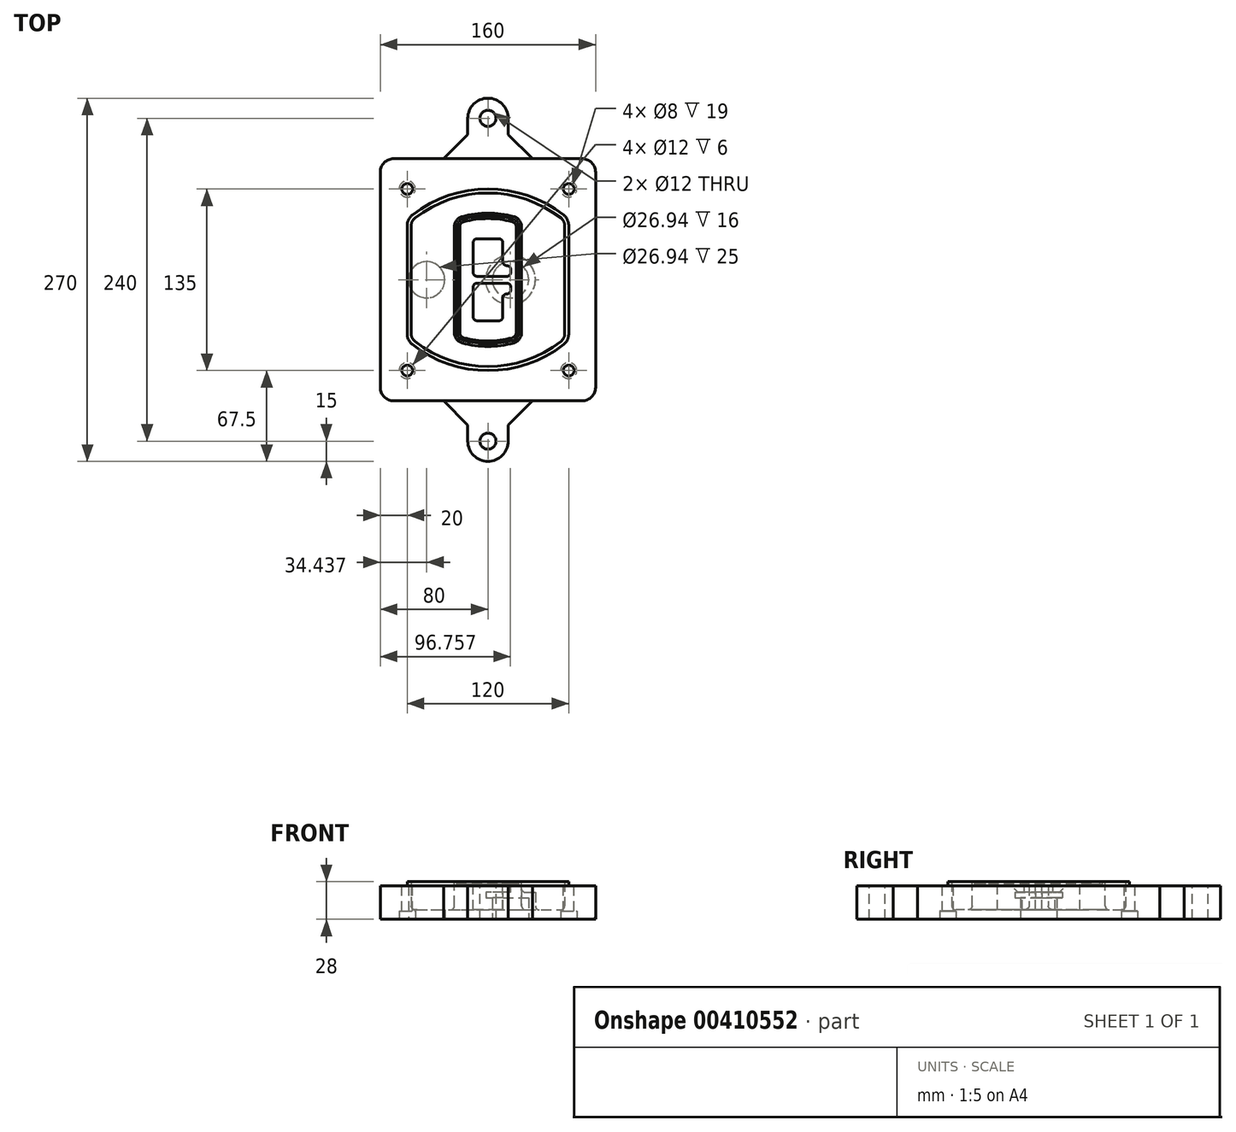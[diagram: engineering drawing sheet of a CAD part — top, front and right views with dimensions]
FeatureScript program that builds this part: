
annotation { "Feature Type Name" : "Feature", "Feature Type Description" : "" }
export const myFeature = defineFeature(function(context is Context, id is Id, definition is map)
    precondition{}
    {
        {
            var Q0;
            Q0=qCreatedBy(makeId("Top.planeOp"),FACE);
            var sketch = newSketch(context, id + "F0", { "sketchPlane" : qUnion([Q0])});
            skPoint(sketch, "E0.rect.middle", {"position": v(0, 0) * mm});
            skLineSegment(sketch, "E1.bottom", {"start": v(-70, -90) * mm, "end": v(70, -90) * mm});
            skLineSegment(sketch, "E1.top", {"start": v(-70, 90) * mm, "end": v(70, 90) * mm});
            skLineSegment(sketch, "E1.left", {"start": v(-80, -80) * mm, "end": v(-80, 80) * mm});
            skLineSegment(sketch, "E1.right", {"start": v(80, -80) * mm, "end": v(80, 80) * mm});
            skLineSegment(sketch, "E2", {"start": v(-80, 90) * mm, "end": v(80, -90) * mm, "construction": true});
            skLineSegment(sketch, "E3", {"start": v(80, 90) * mm, "end": v(-80, -90) * mm, "construction": true});
            skCircle(sketch, "E4", {"center": v(-60, 67.5) * mm, "radius": 4 * mm});
            skCircle(sketch, "E5", {"center": v(60, 67.5) * mm, "radius": 4 * mm});
            skCircle(sketch, "E6", {"center": v(60, -67.5) * mm, "radius": 4 * mm});
            skCircle(sketch, "E7", {"center": v(-60, -67.5) * mm, "radius": 4 * mm});
            skLineSegment(sketch, "E8", {"start": v(-60, 67.5) * mm, "end": v(60, 67.5) * mm, "construction": true});
            skLineSegment(sketch, "E9", {"start": v(60, 67.5) * mm, "end": v(60, -67.5) * mm, "construction": true});
            skLineSegment(sketch, "E10", {"start": v(60, -67.5) * mm, "end": v(-60, -67.5) * mm, "construction": true});
            skLineSegment(sketch, "E11", {"start": v(-60, -67.5) * mm, "end": v(-60, 67.5) * mm, "construction": true});
            skLineSegment(sketch, "E12", {"start": v(-60, 40.3) * mm, "end": v(-60, -40.3) * mm});
            skLineSegment(sketch, "E13", {"start": v(60, 40.3) * mm, "end": v(60, -40.3) * mm});
            skArc(sketch, "E14", {"start": v(56.15, 48.18) * mm, "mid": v(0, 67.5) * mm, "end": v(-56.15, 48.18) * mm});
            skArc(sketch, "E15", {"start": v(-56.15, -48.18) * mm, "mid": v(0, -67.5) * mm, "end": v(56.15, -48.18) * mm});
            skLineSegment(sketch, "E16", {"start": v(-60, 0) * mm, "end": v(60, 0) * mm, "construction": true});
            skPoint(sketch, "E17.visualSharp", {"position": v(-60, -45) * mm});
            skArc(sketch, "E17.filletArc", {"start": v(-60, -40.3) * mm, "mid": v(-58.99, -44.68) * mm, "end": v(-56.15, -48.18) * mm});
            skPoint(sketch, "E18.visualSharp", {"position": v(-60, 45) * mm});
            skArc(sketch, "E18.filletArc", {"start": v(-56.15, 48.18) * mm, "mid": v(-58.99, 44.68) * mm, "end": v(-60, 40.3) * mm});
            skPoint(sketch, "E19.visualSharp", {"position": v(60, 45) * mm});
            skArc(sketch, "E19.filletArc", {"start": v(60, 40.3) * mm, "mid": v(58.99, 44.68) * mm, "end": v(56.15, 48.18) * mm});
            skPoint(sketch, "E20.visualSharp", {"position": v(60, -45) * mm});
            skArc(sketch, "E20.filletArc", {"start": v(56.15, -48.18) * mm, "mid": v(58.99, -44.68) * mm, "end": v(60, -40.3) * mm});
            skPoint(sketch, "E21.visualSharp", {"position": v(-80, 90) * mm});
            skArc(sketch, "E21.filletArc", {"start": v(-70, 90) * mm, "mid": v(-77.07, 87.07) * mm, "end": v(-80, 80) * mm});
            skPoint(sketch, "E22.visualSharp", {"position": v(80, 90) * mm});
            skArc(sketch, "E22.filletArc", {"start": v(80, 80) * mm, "mid": v(77.07, 87.07) * mm, "end": v(70, 90) * mm});
            skPoint(sketch, "E23.visualSharp", {"position": v(80, -90) * mm});
            skArc(sketch, "E23.filletArc", {"start": v(70, -90) * mm, "mid": v(77.07, -87.07) * mm, "end": v(80, -80) * mm});
            skPoint(sketch, "E24.visualSharp", {"position": v(-80, -90) * mm});
            skArc(sketch, "E24.filletArc", {"start": v(-80, -80) * mm, "mid": v(-77.07, -87.07) * mm, "end": v(-70, -90) * mm});
            skArc(sketch, "E25.0", {"start": v(57, 40.3) * mm, "mid": v(56.3, 43.36) * mm, "end": v(54.3, 45.81) * mm});
            skLineSegment(sketch, "E25.1", {"start": v(57, 40.3) * mm, "end": v(57, -40.3) * mm});
            skArc(sketch, "E25.2", {"start": v(54.3, -45.81) * mm, "mid": v(56.3, -43.36) * mm, "end": v(57, -40.3) * mm});
            skArc(sketch, "E25.3", {"start": v(-54.3, -45.81) * mm, "mid": v(0, -64.5) * mm, "end": v(54.3, -45.81) * mm});
            skArc(sketch, "E25.4", {"start": v(-57, -40.3) * mm, "mid": v(-56.3, -43.36) * mm, "end": v(-54.3, -45.81) * mm});
            skArc(sketch, "E25.5", {"start": v(54.3, 45.81) * mm, "mid": v(0, 64.5) * mm, "end": v(-54.3, 45.81) * mm});
            skLineSegment(sketch, "E25.6", {"start": v(-57, 40.3) * mm, "end": v(-57, -40.3) * mm});
            skArc(sketch, "E25.7", {"start": v(-54.3, 45.81) * mm, "mid": v(-56.3, 43.36) * mm, "end": v(-57, 40.3) * mm});
            skArc(sketch, "E26.0", {"start": v(-58.62, 51.33) * mm, "mid": v(-62.58, 46.43) * mm, "end": v(-64, 40.3) * mm});
            skArc(sketch, "E26.1", {"start": v(58.62, 51.33) * mm, "mid": v(0, 71.5) * mm, "end": v(-58.62, 51.33) * mm});
            skArc(sketch, "E26.2", {"start": v(64, 40.3) * mm, "mid": v(62.58, 46.43) * mm, "end": v(58.62, 51.33) * mm});
            skLineSegment(sketch, "E26.3", {"start": v(64, 40.3) * mm, "end": v(64, -40.3) * mm});
            skArc(sketch, "E26.4", {"start": v(58.62, -51.33) * mm, "mid": v(62.58, -46.43) * mm, "end": v(64, -40.3) * mm});
            skLineSegment(sketch, "E26.5", {"start": v(-64, 40.3) * mm, "end": v(-64, -40.3) * mm});
            skArc(sketch, "E26.6", {"start": v(-58.62, -51.33) * mm, "mid": v(0, -71.5) * mm, "end": v(58.62, -51.33) * mm});
            skArc(sketch, "E26.7", {"start": v(-64, -40.3) * mm, "mid": v(-62.58, -46.43) * mm, "end": v(-58.62, -51.33) * mm});
            skSolve(sketch);
        }
        {
            var Q0;
            Q0=makeQuery(id+"F0.imprint","IMPRINT",FACE,{"disambiguationData":[TD([[makeQuery(id+"F0.imprint","IMPRINT",EDGE,{"derivedFrom":sQuery(id+"F0.wireOp",EDGE,"E1.bottom")}),1.0]])]});
            var Q1;
            Q1=makeQuery(id+"F0.imprint","IMPRINT",FACE,{"disambiguationData":[TD([[makeQuery(id+"F0.imprint","IMPRINT",EDGE,{"derivedFrom":sQuery(id+"F0.wireOp",EDGE,"E12")}),1.0]])]});
            var Q2;
            Q2=makeQuery(id+"F0.imprint","IMPRINT",FACE,{"disambiguationData":[TD([[makeQuery(id+"F0.imprint","IMPRINT",EDGE,{"derivedFrom":sQuery(id+"F0.wireOp",EDGE,"E25.0")}),1.0]])]});
            var Q3;
            Q3=makeQuery(id+"F0.imprint","IMPRINT",FACE,{"disambiguationData":[TD([[makeQuery(id+"F0.imprint","IMPRINT",EDGE,{"derivedFrom":sQuery(id+"F0.wireOp",EDGE,"E12")}),-1.0]])]});
            extrude(context, id + "F1", {"entities" : qUnion([Q0, Q1, Q2, Q3]), "oppositeDirection" : true, "depth" : 25 * mm});
        }
        {
            var Q0;
            Q0=makeQuery(id+"F0.imprint","IMPRINT",FACE,{"disambiguationData":[TD([[makeQuery(id+"F0.imprint","IMPRINT",EDGE,{"derivedFrom":sQuery(id+"F0.wireOp",EDGE,"E12")}),1.0]])]});
            extrude(context, id + "F2", {"entities" : qUnion([Q0]), "operationType" : NewBodyOperationType.ADD, "depth" : 3 * mm});
        }
        {
            var Q0;
            Q0=makeQuery(id+"F0.imprint","IMPRINT",FACE,{"disambiguationData":[TD([[makeQuery(id+"F0.imprint","IMPRINT",EDGE,{"derivedFrom":sQuery(id+"F0.wireOp",EDGE,"E25.0")}),1.0]])]});
            extrude(context, id + "F3", {"entities" : qUnion([Q0]), "operationType" : NewBodyOperationType.REMOVE, "oppositeDirection" : true, "depth" : 18 * mm});
        }
        {
            var Q0;
            Q0=makeQuery(id+"F2.opExtrude","CAP_FACE",FACE,{"disambiguationData":[OSD([sQuery(id+"F0.wireOp",EDGE,"E12"),sQuery(id+"F0.wireOp",EDGE,"E13"),sQuery(id+"F0.wireOp",EDGE,"E14"),sQuery(id+"F0.wireOp",EDGE,"E15"),sQuery(id+"F0.wireOp",EDGE,"E17.filletArc"),sQuery(id+"F0.wireOp",EDGE,"E18.filletArc"),sQuery(id+"F0.wireOp",EDGE,"E19.filletArc"),sQuery(id+"F0.wireOp",EDGE,"E20.filletArc"),sQuery(id+"F0.wireOp",EDGE,"E25.0"),sQuery(id+"F0.wireOp",EDGE,"E25.1"),sQuery(id+"F0.wireOp",EDGE,"E25.2"),sQuery(id+"F0.wireOp",EDGE,"E25.3"),sQuery(id+"F0.wireOp",EDGE,"E25.4"),sQuery(id+"F0.wireOp",EDGE,"E25.5"),sQuery(id+"F0.wireOp",EDGE,"E25.6"),sQuery(id+"F0.wireOp",EDGE,"E25.7")])],"isStart":false});
            var sketch = newSketch(context, id + "F4", { "sketchPlane" : qUnion([Q0])});
            skArc(sketch, "E27.0", {"start": v(-19.08, -46.97) * mm, "mid": v(0, -49.5) * mm, "end": v(19.08, -46.97) * mm});
            skArc(sketch, "E28.0", {"start": v(19.08, 46.97) * mm, "mid": v(0, 49.5) * mm, "end": v(-19.08, 46.97) * mm});
            skLineSegment(sketch, "E29", {"start": v(-25, 39.25) * mm, "end": v(-25, -39.25) * mm});
            skLineSegment(sketch, "E30", {"start": v(25, 39.25) * mm, "end": v(25, -39.25) * mm});
            skLineSegment(sketch, "E31", {"start": v(-25, 45.1) * mm, "end": v(25, 45.1) * mm, "construction": true});
            skLineSegment(sketch, "E32", {"start": v(-25, -45.1) * mm, "end": v(25, -45.1) * mm, "construction": true});
            skPoint(sketch, "E33.visualSharp", {"position": v(-25, 45.1) * mm});
            skArc(sketch, "E33.filletArc", {"start": v(-19.08, 46.97) * mm, "mid": v(-23.35, 44.11) * mm, "end": v(-25, 39.25) * mm});
            skPoint(sketch, "E34.visualSharp", {"position": v(25, 45.1) * mm});
            skArc(sketch, "E34.filletArc", {"start": v(25, 39.25) * mm, "mid": v(23.35, 44.11) * mm, "end": v(19.08, 46.97) * mm});
            skPoint(sketch, "E35.visualSharp", {"position": v(25, -45.1) * mm});
            skArc(sketch, "E35.filletArc", {"start": v(19.08, -46.97) * mm, "mid": v(23.35, -44.11) * mm, "end": v(25, -39.25) * mm});
            skPoint(sketch, "E36.visualSharp", {"position": v(-25, -45.1) * mm});
            skArc(sketch, "E36.filletArc", {"start": v(-25, -39.25) * mm, "mid": v(-23.35, -44.11) * mm, "end": v(-19.08, -46.97) * mm});
            skArc(sketch, "E37.0", {"start": v(54.3, 45.81) * mm, "mid": v(0, 64.5) * mm, "end": v(-54.3, 45.81) * mm});
            skArc(sketch, "E37.1", {"start": v(-54.3, 45.81) * mm, "mid": v(-56.3, 43.36) * mm, "end": v(-57, 40.3) * mm});
            skLineSegment(sketch, "E37.2", {"start": v(-57, 40.3) * mm, "end": v(-57, -40.3) * mm});
            skArc(sketch, "E37.3", {"start": v(-57, -40.3) * mm, "mid": v(-56.3, -43.36) * mm, "end": v(-54.3, -45.81) * mm});
            skArc(sketch, "E37.4", {"start": v(-54.3, -45.81) * mm, "mid": v(0, -64.5) * mm, "end": v(54.3, -45.81) * mm});
            skArc(sketch, "E37.5", {"start": v(54.3, -45.81) * mm, "mid": v(56.3, -43.36) * mm, "end": v(57, -40.3) * mm});
            skLineSegment(sketch, "E37.6", {"start": v(57, 40.3) * mm, "end": v(57, -40.3) * mm});
            skArc(sketch, "E37.7", {"start": v(57, 40.3) * mm, "mid": v(56.3, 43.36) * mm, "end": v(54.3, 45.81) * mm});
            skLineSegment(sketch, "E38.0", {"start": v(23, 39.25) * mm, "end": v(23, -39.25) * mm});
            skArc(sketch, "E38.1", {"start": v(18.56, -45.04) * mm, "mid": v(21.76, -42.9) * mm, "end": v(23, -39.25) * mm});
            skArc(sketch, "E38.2", {"start": v(-18.56, -45.04) * mm, "mid": v(0, -47.5) * mm, "end": v(18.56, -45.04) * mm});
            skArc(sketch, "E38.3", {"start": v(-23, -39.25) * mm, "mid": v(-21.76, -42.9) * mm, "end": v(-18.56, -45.04) * mm});
            skLineSegment(sketch, "E38.4", {"start": v(-23, 39.25) * mm, "end": v(-23, -39.25) * mm});
            skArc(sketch, "E38.5", {"start": v(23, 39.25) * mm, "mid": v(21.76, 42.9) * mm, "end": v(18.56, 45.04) * mm});
            skArc(sketch, "E38.6", {"start": v(-18.56, 45.04) * mm, "mid": v(-21.76, 42.9) * mm, "end": v(-23, 39.25) * mm});
            skArc(sketch, "E38.7", {"start": v(18.56, 45.04) * mm, "mid": v(0, 47.5) * mm, "end": v(-18.56, 45.04) * mm});
            skArc(sketch, "E39.0", {"start": v(21, 39.25) * mm, "mid": v(20.18, 41.68) * mm, "end": v(18.04, 43.1) * mm});
            skLineSegment(sketch, "E39.1", {"start": v(21, 39.25) * mm, "end": v(21, -39.25) * mm});
            skArc(sketch, "E39.2", {"start": v(18.04, -43.1) * mm, "mid": v(20.18, -41.68) * mm, "end": v(21, -39.25) * mm});
            skArc(sketch, "E39.3", {"start": v(-18.04, -43.1) * mm, "mid": v(0, -45.5) * mm, "end": v(18.04, -43.1) * mm});
            skArc(sketch, "E39.4", {"start": v(-21, -39.25) * mm, "mid": v(-20.18, -41.68) * mm, "end": v(-18.04, -43.1) * mm});
            skArc(sketch, "E39.5", {"start": v(18.04, 43.1) * mm, "mid": v(0, 45.5) * mm, "end": v(-18.04, 43.1) * mm});
            skLineSegment(sketch, "E39.6", {"start": v(-21, 39.25) * mm, "end": v(-21, -39.25) * mm});
            skArc(sketch, "E39.7", {"start": v(-18.04, 43.1) * mm, "mid": v(-20.18, 41.68) * mm, "end": v(-21, 39.25) * mm});
            skLineSegment(sketch, "E40", {"start": v(-25, 0) * mm, "end": v(25, 0) * mm, "construction": true});
            skLineSegment(sketch, "E41", {"start": v(-11, 5.5) * mm, "end": v(-11, 27.5) * mm});
            skLineSegment(sketch, "E42", {"start": v(-8, 30.5) * mm, "end": v(8, 30.5) * mm});
            skLineSegment(sketch, "E43", {"start": v(11, 27.5) * mm, "end": v(11, 13.5) * mm});
            skLineSegment(sketch, "E44", {"start": v(14, 10.5) * mm, "end": v(14, 10.5) * mm});
            skLineSegment(sketch, "E45", {"start": v(17, 7.5) * mm, "end": v(17, 5.5) * mm});
            skLineSegment(sketch, "E46", {"start": v(14, 2.5) * mm, "end": v(-8, 2.5) * mm});
            skPoint(sketch, "E47.visualSharp", {"position": v(-11, 30.5) * mm});
            skArc(sketch, "E47.filletArc", {"start": v(-8, 30.5) * mm, "mid": v(-10.12, 29.62) * mm, "end": v(-11, 27.5) * mm});
            skPoint(sketch, "E48.visualSharp", {"position": v(11, 30.5) * mm});
            skArc(sketch, "E48.filletArc", {"start": v(11, 27.5) * mm, "mid": v(10.12, 29.62) * mm, "end": v(8, 30.5) * mm});
            skPoint(sketch, "E49.visualSharp", {"position": v(11, 10.5) * mm});
            skArc(sketch, "E49.filletArc", {"start": v(11, 13.5) * mm, "mid": v(11.88, 11.38) * mm, "end": v(14, 10.5) * mm});
            skPoint(sketch, "E50.visualSharp", {"position": v(17, 10.5) * mm});
            skArc(sketch, "E50.filletArc", {"start": v(17, 7.5) * mm, "mid": v(16.12, 9.62) * mm, "end": v(14, 10.5) * mm});
            skPoint(sketch, "E51.visualSharp", {"position": v(17, 2.5) * mm});
            skArc(sketch, "E51.filletArc", {"start": v(14, 2.5) * mm, "mid": v(16.12, 3.38) * mm, "end": v(17, 5.5) * mm});
            skPoint(sketch, "E52.visualSharp", {"position": v(-11, 2.5) * mm});
            skArc(sketch, "E52.filletArc", {"start": v(-11, 5.5) * mm, "mid": v(-10.12, 3.38) * mm, "end": v(-8, 2.5) * mm});
            skLineSegment(sketch, "E53.0.MirrorCS", {"start": v(14, -2.5) * mm, "end": v(-8, -2.5) * mm});
            skArc(sketch, "E54.0.MirrorCS", {"start": v(-11, -5.5) * mm, "mid": v(-10.12, -3.38) * mm, "end": v(-8, -2.5) * mm});
            skLineSegment(sketch, "E55.0.MirrorCS", {"start": v(-11, -5.5) * mm, "end": v(-11, -27.5) * mm});
            skArc(sketch, "E56.0.MirrorCS", {"start": v(-8, -30.5) * mm, "mid": v(-10.12, -29.62) * mm, "end": v(-11, -27.5) * mm});
            skLineSegment(sketch, "E57.0.MirrorCS", {"start": v(-8, -30.5) * mm, "end": v(8, -30.5) * mm});
            skArc(sketch, "E58.0.MirrorCS", {"start": v(11, -27.5) * mm, "mid": v(10.12, -29.62) * mm, "end": v(8, -30.5) * mm});
            skLineSegment(sketch, "E59.0.MirrorCS", {"start": v(11, -27.5) * mm, "end": v(11, -13.5) * mm});
            skArc(sketch, "E60.0.MirrorCS", {"start": v(11, -13.5) * mm, "mid": v(11.88, -11.38) * mm, "end": v(14, -10.5) * mm});
            skArc(sketch, "E61.0.MirrorCS", {"start": v(17, -7.5) * mm, "mid": v(16.12, -9.62) * mm, "end": v(14, -10.5) * mm});
            skLineSegment(sketch, "E62.0.MirrorCS", {"start": v(17, -7.5) * mm, "end": v(17, -5.5) * mm});
            skArc(sketch, "E63.0.MirrorCS", {"start": v(14, -2.5) * mm, "mid": v(16.12, -3.38) * mm, "end": v(17, -5.5) * mm});
            skSolve(sketch);
        }
        {
            var Q0;
            Q0=makeQuery(id+"F4.imprint","IMPRINT",FACE,{"disambiguationData":[TD([[makeQuery(id+"F4.imprint","IMPRINT",EDGE,{"derivedFrom":sQuery(id+"F4.wireOp",EDGE,"E27.0")}),1.0]])]});
            var Q1;
            Q1=makeQuery(id+"F4.imprint","IMPRINT",FACE,{"disambiguationData":[TD([[makeQuery(id+"F4.imprint","IMPRINT",EDGE,{"derivedFrom":sQuery(id+"F4.wireOp",EDGE,"E38.0")}),-1.0]])]});
            var Q2;
            Q2=makeQuery(id+"F4.imprint","IMPRINT",FACE,{"disambiguationData":[TD([[makeQuery(id+"F4.imprint","IMPRINT",EDGE,{"derivedFrom":sQuery(id+"F4.wireOp",EDGE,"E39.0")}),1.0]])]});
            extrude(context, id + "F5", {"entities" : qUnion([Q0, Q1, Q2]), "operationType" : NewBodyOperationType.ADD, "endBound" : BoundingType.UP_TO_NEXT, "oppositeDirection" : true, "depth" : 25 * mm});
        }
        {
            var Q0;
            Q0=makeQuery(id+"F4.imprint","IMPRINT",FACE,{"disambiguationData":[TD([[makeQuery(id+"F4.imprint","IMPRINT",EDGE,{"derivedFrom":sQuery(id+"F4.wireOp",EDGE,"E38.0")}),-1.0]])]});
            extrude(context, id + "F6", {"entities" : qUnion([Q0]), "operationType" : NewBodyOperationType.REMOVE, "oppositeDirection" : true, "depth" : 2 * mm});
        }
        {
            var Q0;
            Q0=makeQuery(id+"F1.opExtrude","CAP_FACE",FACE,{"disambiguationData":[OSD([sQuery(id+"F0.wireOp",EDGE,"E1.bottom"),sQuery(id+"F0.wireOp",EDGE,"E1.top"),sQuery(id+"F0.wireOp",EDGE,"E1.left"),sQuery(id+"F0.wireOp",EDGE,"E1.right"),sQuery(id+"F0.wireOp",EDGE,"E4"),sQuery(id+"F0.wireOp",EDGE,"E5"),sQuery(id+"F0.wireOp",EDGE,"E6"),sQuery(id+"F0.wireOp",EDGE,"E7"),sQuery(id+"F0.wireOp",EDGE,"E21.filletArc"),sQuery(id+"F0.wireOp",EDGE,"E22.filletArc"),sQuery(id+"F0.wireOp",EDGE,"E23.filletArc"),sQuery(id+"F0.wireOp",EDGE,"E24.filletArc")])],"isStart":false});
            var sketch = newSketch(context, id + "F7", { "sketchPlane" : qUnion([Q0])});
            skCircle(sketch, "E64", {"center": v(16.76, 0) * mm, "radius": 13.47 * mm});
            skCircle(sketch, "E65", {"center": v(-45.56, 0) * mm, "radius": 13.47 * mm});
            skLineSegment(sketch, "E66", {"start": v(80, 0) * mm, "end": v(-80, 0) * mm});
            skCircle(sketch, "E67", {"center": v(16.76, 0) * mm, "radius": 18.47 * mm});
            skCircle(sketch, "E68", {"center": v(60, -67.5) * mm, "radius": 6 * mm});
            skCircle(sketch, "E69", {"center": v(-60, -67.5) * mm, "radius": 6 * mm});
            skCircle(sketch, "E70", {"center": v(-60, 67.5) * mm, "radius": 6 * mm});
            skCircle(sketch, "E71", {"center": v(60, 67.5) * mm, "radius": 6 * mm});
            skSolve(sketch);
        }
        {
            var Q0;
            {var subQ1=sQuery(id+"F7.wireOp",EDGE,"E66");var subQ4=sQuery(id+"F7.wireOp",EDGE,"E64");var subQ6=makeQuery(id+"F7.imprint","INTERSECT",VERTEX,{"disambiguationData":[OD(0.0)],"derivedFrom":[subQ4,subQ1]});Q0=makeQuery(id+"F7.imprint","IMPRINT",FACE,{"disambiguationData":[TD([[makeQuery(id+"F7.imprint","IMPRINT",EDGE,{"disambiguationData":[TD([[subQ6,-1.0]])],"derivedFrom":subQ4}),-1.0]])]});}
            var Q1;
            {var subQ0=sQuery(id+"F7.wireOp",EDGE,"E66");var subQ1=sQuery(id+"F7.wireOp",EDGE,"E64");var subQ3=makeQuery(id+"F7.imprint","INTERSECT",VERTEX,{"disambiguationData":[OD(0.0)],"derivedFrom":[subQ1,subQ0]});Q1=makeQuery(id+"F7.imprint","IMPRINT",FACE,{"disambiguationData":[TD([[makeQuery(id+"F7.imprint","IMPRINT",EDGE,{"disambiguationData":[TD([[subQ3,-1.0]])],"derivedFrom":subQ1}),1.0]])]});}
            var Q2;
            {var subQ0=sQuery(id+"F7.wireOp",EDGE,"E66");var subQ1=sQuery(id+"F7.wireOp",EDGE,"E64");var subQ3=makeQuery(id+"F7.imprint","INTERSECT",VERTEX,{"disambiguationData":[OD(0.0)],"derivedFrom":[subQ1,subQ0]});Q2=makeQuery(id+"F7.imprint","IMPRINT",FACE,{"disambiguationData":[TD([[makeQuery(id+"F7.imprint","IMPRINT",EDGE,{"disambiguationData":[TD([[subQ3,1.0]])],"derivedFrom":subQ1}),1.0]])]});}
            var Q3;
            {var subQ1=sQuery(id+"F7.wireOp",EDGE,"E66");var subQ4=sQuery(id+"F7.wireOp",EDGE,"E64");var subQ6=makeQuery(id+"F7.imprint","INTERSECT",VERTEX,{"disambiguationData":[OD(0.0)],"derivedFrom":[subQ4,subQ1]});Q3=makeQuery(id+"F7.imprint","IMPRINT",FACE,{"disambiguationData":[TD([[makeQuery(id+"F7.imprint","IMPRINT",EDGE,{"disambiguationData":[TD([[subQ6,1.0]])],"derivedFrom":subQ4}),-1.0]])]});}
            extrude(context, id + "F8", {"entities" : qUnion([Q0, Q1, Q2, Q3]), "operationType" : NewBodyOperationType.ADD, "oppositeDirection" : true, "depth" : 20 * mm});
        }
        {
            var Q0;
            {var subQ0=sQuery(id+"F7.wireOp",EDGE,"E66");var subQ1=sQuery(id+"F7.wireOp",EDGE,"E64");var subQ3=makeQuery(id+"F7.imprint","INTERSECT",VERTEX,{"disambiguationData":[OD(0.0)],"derivedFrom":[subQ1,subQ0]});Q0=makeQuery(id+"F7.imprint","IMPRINT",FACE,{"disambiguationData":[TD([[makeQuery(id+"F7.imprint","IMPRINT",EDGE,{"disambiguationData":[TD([[subQ3,-1.0]])],"derivedFrom":subQ1}),1.0]])]});}
            var Q1;
            {var subQ0=sQuery(id+"F7.wireOp",EDGE,"E66");var subQ1=sQuery(id+"F7.wireOp",EDGE,"E64");var subQ3=makeQuery(id+"F7.imprint","INTERSECT",VERTEX,{"disambiguationData":[OD(0.0)],"derivedFrom":[subQ1,subQ0]});Q1=makeQuery(id+"F7.imprint","IMPRINT",FACE,{"disambiguationData":[TD([[makeQuery(id+"F7.imprint","IMPRINT",EDGE,{"disambiguationData":[TD([[subQ3,1.0]])],"derivedFrom":subQ1}),1.0]])]});}
            extrude(context, id + "F9", {"entities" : qUnion([Q0, Q1]), "operationType" : NewBodyOperationType.REMOVE, "oppositeDirection" : true, "depth" : 16 * mm});
        }
        {
            var Q0;
            {var subQ0=sQuery(id+"F7.wireOp",EDGE,"E66");var subQ1=sQuery(id+"F7.wireOp",EDGE,"E65");var subQ3=makeQuery(id+"F7.imprint","INTERSECT",VERTEX,{"disambiguationData":[OD(0.0)],"derivedFrom":[subQ1,subQ0]});Q0=makeQuery(id+"F7.imprint","IMPRINT",FACE,{"disambiguationData":[TD([[makeQuery(id+"F7.imprint","IMPRINT",EDGE,{"disambiguationData":[TD([[subQ3,-1.0]])],"derivedFrom":subQ1}),1.0]])]});}
            var Q1;
            {var subQ0=sQuery(id+"F7.wireOp",EDGE,"E66");var subQ1=sQuery(id+"F7.wireOp",EDGE,"E65");var subQ3=makeQuery(id+"F7.imprint","INTERSECT",VERTEX,{"disambiguationData":[OD(0.0)],"derivedFrom":[subQ1,subQ0]});Q1=makeQuery(id+"F7.imprint","IMPRINT",FACE,{"disambiguationData":[TD([[makeQuery(id+"F7.imprint","IMPRINT",EDGE,{"disambiguationData":[TD([[subQ3,1.0]])],"derivedFrom":subQ1}),1.0]])]});}
            extrude(context, id + "F10", {"entities" : qUnion([Q0, Q1]), "operationType" : NewBodyOperationType.REMOVE, "oppositeDirection" : true, "depth" : 25 * mm});
        }
        {
            var Q0;
            Q0=makeQuery(id+"F7.imprint","IMPRINT",FACE,{"disambiguationData":[TD([[makeQuery(id+"F7.imprint","IMPRINT",EDGE,{"derivedFrom":sQuery(id+"F7.wireOp",EDGE,"E68")}),1.0]])]});
            var Q1;
            Q1=makeQuery(id+"F7.imprint","IMPRINT",FACE,{"disambiguationData":[TD([[makeQuery(id+"F7.imprint","IMPRINT",EDGE,{"derivedFrom":makeQuery(id+"F1.opExtrude","CAP_EDGE",EDGE,{"disambiguationData":[OSD([sQuery(id+"F0.wireOp",EDGE,"E5")])],"isStart":false})}),-1.0]])]});
            var Q2;
            Q2=makeQuery(id+"F7.imprint","IMPRINT",FACE,{"disambiguationData":[TD([[makeQuery(id+"F7.imprint","IMPRINT",EDGE,{"derivedFrom":sQuery(id+"F7.wireOp",EDGE,"E69")}),1.0]])]});
            var Q3;
            Q3=makeQuery(id+"F7.imprint","IMPRINT",FACE,{"disambiguationData":[TD([[makeQuery(id+"F7.imprint","IMPRINT",EDGE,{"derivedFrom":makeQuery(id+"F1.opExtrude","CAP_EDGE",EDGE,{"disambiguationData":[OSD([sQuery(id+"F0.wireOp",EDGE,"E4")])],"isStart":false})}),-1.0]])]});
            var Q4;
            Q4=makeQuery(id+"F7.imprint","IMPRINT",FACE,{"disambiguationData":[TD([[makeQuery(id+"F7.imprint","IMPRINT",EDGE,{"derivedFrom":sQuery(id+"F7.wireOp",EDGE,"E70")}),1.0]])]});
            var Q5;
            Q5=makeQuery(id+"F7.imprint","IMPRINT",FACE,{"disambiguationData":[TD([[makeQuery(id+"F7.imprint","IMPRINT",EDGE,{"derivedFrom":makeQuery(id+"F1.opExtrude","CAP_EDGE",EDGE,{"disambiguationData":[OSD([sQuery(id+"F0.wireOp",EDGE,"E7")])],"isStart":false})}),-1.0]])]});
            var Q6;
            Q6=makeQuery(id+"F7.imprint","IMPRINT",FACE,{"disambiguationData":[TD([[makeQuery(id+"F7.imprint","IMPRINT",EDGE,{"derivedFrom":sQuery(id+"F7.wireOp",EDGE,"E71")}),1.0]])]});
            var Q7;
            Q7=makeQuery(id+"F7.imprint","IMPRINT",FACE,{"disambiguationData":[TD([[makeQuery(id+"F7.imprint","IMPRINT",EDGE,{"derivedFrom":makeQuery(id+"F1.opExtrude","CAP_EDGE",EDGE,{"disambiguationData":[OSD([sQuery(id+"F0.wireOp",EDGE,"E6")])],"isStart":false})}),-1.0]])]});
            extrude(context, id + "F11", {"entities" : qUnion([Q0, Q1, Q2, Q3, Q4, Q5, Q6, Q7]), "operationType" : NewBodyOperationType.REMOVE, "oppositeDirection" : true, "depth" : 6 * mm});
        }
        {
            var Q0;
            Q0=makeQuery(id+"F9.boolean.opBoolean","COPY",FACE,{"derivedFrom":makeQuery(id+"F9.opExtrude","CAP_FACE",FACE,{"disambiguationData":[OSD([sQuery(id+"F7.wireOp",EDGE,"E64")])],"isStart":false})});
            var sketch = newSketch(context, id + "F12", { "sketchPlane" : qUnion([Q0])});
            skArc(sketch, "E72.0", {"start": v(11, 17.55) * mm, "mid": v(2.57, 11.82) * mm, "end": v(-1.54, 2.5) * mm});
            skArc(sketch, "E72.1", {"start": v(-1.54, -2.5) * mm, "mid": v(2.57, -11.82) * mm, "end": v(11, -17.55) * mm});
            skLineSegment(sketch, "E73", {"start": v(-1.54, -2.5) * mm, "end": v(14, -2.5) * mm});
            skLineSegment(sketch, "E74.0", {"start": v(14, 2.5) * mm, "end": v(-1.54, 2.5) * mm});
            skArc(sketch, "E74.1", {"start": v(14, 2.5) * mm, "mid": v(16.12, 3.38) * mm, "end": v(17, 5.5) * mm});
            skLineSegment(sketch, "E74.2", {"start": v(17, 7.5) * mm, "end": v(17, 5.5) * mm});
            skArc(sketch, "E74.3", {"start": v(17, 7.5) * mm, "mid": v(16.12, 9.62) * mm, "end": v(14, 10.5) * mm});
            skArc(sketch, "E74.4", {"start": v(11, 13.5) * mm, "mid": v(11.88, 11.38) * mm, "end": v(14, 10.5) * mm});
            skLineSegment(sketch, "E74.5", {"start": v(11, 17.55) * mm, "end": v(11, 13.5) * mm});
            skLineSegment(sketch, "E74.7", {"start": v(14, -2.5) * mm, "end": v(-1.54, -2.5) * mm});
            skArc(sketch, "E74.8", {"start": v(14, -2.5) * mm, "mid": v(16.12, -3.38) * mm, "end": v(17, -5.5) * mm});
            skLineSegment(sketch, "E74.9", {"start": v(17, -7.5) * mm, "end": v(17, -5.5) * mm});
            skArc(sketch, "E74.10", {"start": v(17, -7.5) * mm, "mid": v(16.12, -9.62) * mm, "end": v(14, -10.5) * mm});
            skArc(sketch, "E74.11", {"start": v(11, -13.5) * mm, "mid": v(11.88, -11.38) * mm, "end": v(14, -10.5) * mm});
            skLineSegment(sketch, "E74.12", {"start": v(11, -17.55) * mm, "end": v(11, -13.5) * mm});
            skPoint(sketch, "E75.orphan", {"position": v(11, -27.5) * mm});
            skPoint(sketch, "E76.orphan", {"position": v(-8, -2.5) * mm});
            skPoint(sketch, "E77.orphan", {"position": v(-8, 2.5) * mm});
            skPoint(sketch, "E78.orphan", {"position": v(11, 27.5) * mm});
            skSolve(sketch);
        }
        {
            var Q0;
            {var subQ7=sQuery(id+"F12.wireOp",EDGE,"E72.0");var subQ14=sQuery(id+"F12.wireOp",EDGE,"E72.1");var subQ16=sQuery(id+"F12.wireOp",EDGE,"E74.1");var subQ18=sQuery(id+"F12.wireOp",EDGE,"E74.8");Q0=qUnion([makeQuery(id+"F12.imprint","IMPRINT",FACE,{"disambiguationData":[TD([[makeQuery(id+"F12.imprint","IMPRINT",EDGE,{"derivedFrom":subQ7}),1.0]])]}),makeQuery(id+"F12.imprint","IMPRINT",FACE,{"disambiguationData":[TD([[makeQuery(id+"F12.imprint","IMPRINT",EDGE,{"derivedFrom":subQ14}),1.0]])]}),makeQuery(id+"F12.imprint","IMPRINT",FACE,{"disambiguationData":[TD([[makeQuery(id+"F12.imprint","IMPRINT",EDGE,{"derivedFrom":subQ16}),1.0]])]}),makeQuery(id+"F12.imprint","IMPRINT",FACE,{"disambiguationData":[TD([[makeQuery(id+"F12.imprint","IMPRINT",EDGE,{"derivedFrom":subQ18}),-1.0]])]})]);}
            var Q1;
            Q1=makeQuery(id+"F5.boolean.opBoolean","SPLIT",FACE,{"disambiguationData":[TD([makeQuery(id+"F5.opExtrude","SWEPT_FACE",FACE,{"disambiguationData":[OSD([sQuery(id+"F4.wireOp",EDGE,"E41")])]})])],"derivedFrom":makeQuery(id+"F3.boolean.opBoolean","COPY",FACE,{"derivedFrom":makeQuery(id+"F3.opExtrude","CAP_FACE",FACE,{"disambiguationData":[OSD([sQuery(id+"F0.wireOp",EDGE,"E25.0"),sQuery(id+"F0.wireOp",EDGE,"E25.1"),sQuery(id+"F0.wireOp",EDGE,"E25.2"),sQuery(id+"F0.wireOp",EDGE,"E25.3"),sQuery(id+"F0.wireOp",EDGE,"E25.4"),sQuery(id+"F0.wireOp",EDGE,"E25.5"),sQuery(id+"F0.wireOp",EDGE,"E25.6"),sQuery(id+"F0.wireOp",EDGE,"E25.7")])],"isStart":false})})});
            extrude(context, id + "F13", {"entities" : qUnion([Q0]), "operationType" : NewBodyOperationType.REMOVE, "endBound" : BoundingType.UP_TO_SURFACE, "endBoundEntityFace" : qUnion([Q1]), "depth" : 25 * mm});
        }
        {
            var Q0;
            Q0=makeQuery(id+"F3.boolean.opBoolean","COPY",EDGE,{"derivedFrom":makeQuery(id+"F3.opExtrude","CAP_EDGE",EDGE,{"disambiguationData":[OSD([sQuery(id+"F0.wireOp",EDGE,"E25.6")])],"isStart":false})});
            var Q1;
            Q1=makeQuery(id+"F8.boolean.opBoolean","INTERSECT",EDGE,{"derivedFrom":[makeQuery(id+"F5.opExtrude","SWEPT_FACE",FACE,{"disambiguationData":[OSD([sQuery(id+"F4.wireOp",EDGE,"E30")])]}),makeQuery(id+"F8.opExtrude","CAP_FACE",FACE,{"disambiguationData":[OSD([sQuery(id+"F7.wireOp",EDGE,"E67")])],"isStart":false})]});
            var Q2;
            Q2=makeQuery(id+"F8.boolean.opBoolean","INTERSECT",EDGE,{"disambiguationData":[OD(1.0)],"derivedFrom":[makeQuery(id+"F5.opExtrude","SWEPT_FACE",FACE,{"disambiguationData":[OSD([sQuery(id+"F4.wireOp",EDGE,"E30")])]}),makeQuery(id+"F8.opExtrude","SWEPT_FACE",FACE,{"disambiguationData":[OSD([sQuery(id+"F7.wireOp",EDGE,"E67")])]})]});
            var Q3;
            {var subQ0=sQuery(id+"F4.wireOp",EDGE,"E30");Q3=makeQuery(id+"F8.boolean.opBoolean","SPLIT",EDGE,{"disambiguationData":[TD([makeQuery(id+"F5.opExtrude","SWEPT_FACE",FACE,{"disambiguationData":[OSD([sQuery(id+"F4.wireOp",EDGE,"E35.filletArc")])]})])],"derivedFrom":makeQuery(id+"F5.opExtrude","CAP_EDGE",EDGE,{"disambiguationData":[OSD([subQ0])],"isStart":false})});}
            var Q4;
            {var subQ0=sQuery(id+"F0.wireOp",EDGE,"E25.7");var subQ1=sQuery(id+"F0.wireOp",EDGE,"E25.1");var subQ2=sQuery(id+"F0.wireOp",EDGE,"E25.6");var subQ3=sQuery(id+"F0.wireOp",EDGE,"E25.5");var subQ4=sQuery(id+"F0.wireOp",EDGE,"E25.4");var subQ5=sQuery(id+"F0.wireOp",EDGE,"E25.0");var subQ6=sQuery(id+"F0.wireOp",EDGE,"E25.2");var subQ7=sQuery(id+"F0.wireOp",EDGE,"E25.3");Q4=makeQuery(id+"F8.boolean.opBoolean","INTERSECT",EDGE,{"derivedFrom":[makeQuery(id+"F5.boolean.opBoolean","SPLIT",FACE,{"disambiguationData":[TD([makeQuery(id+"F2.opExtrude","SWEPT_FACE",FACE,{"disambiguationData":[OSD([subQ5])]})])],"derivedFrom":makeQuery(id+"F3.boolean.opBoolean","COPY",FACE,{"derivedFrom":makeQuery(id+"F3.opExtrude","CAP_FACE",FACE,{"disambiguationData":[OSD([subQ5,subQ1,subQ6,subQ7,subQ4,subQ3,subQ2,subQ0])],"isStart":false})})}),makeQuery(id+"F8.opExtrude","SWEPT_FACE",FACE,{"disambiguationData":[OSD([sQuery(id+"F7.wireOp",EDGE,"E67")])]})]});}
            var Q5;
            Q5=makeQuery(id+"F8.boolean.opBoolean","INTERSECT",EDGE,{"disambiguationData":[OD(0.0)],"derivedFrom":[makeQuery(id+"F5.opExtrude","SWEPT_FACE",FACE,{"disambiguationData":[OSD([sQuery(id+"F4.wireOp",EDGE,"E30")])]}),makeQuery(id+"F8.opExtrude","SWEPT_FACE",FACE,{"disambiguationData":[OSD([sQuery(id+"F7.wireOp",EDGE,"E67")])]})]});
            fillet(context, id + "F14", {"entities" : qUnion([Q0, Q1, Q2, Q3, Q4, Q5]), "radius" : 3 * mm, "tangentPropagation" : true, "allowEdgeOverflow" : false});
        }
        {
            var Q0;
            Q0=makeQuery(id+"F1.opExtrude","CAP_EDGE",EDGE,{"disambiguationData":[OSD([sQuery(id+"F0.wireOp",EDGE,"E1.bottom")])],"isStart":false});
            fillet(context, id + "F15", {"entities" : qUnion([Q0]), "radius" : 2 * mm, "tangentPropagation" : true, "allowEdgeOverflow" : false});
        }
        {
            var Q0;
            {var subQ0=sQuery(id+"F0.wireOp",EDGE,"E21.filletArc");var subQ1=sQuery(id+"F0.wireOp",EDGE,"E7");var subQ2=sQuery(id+"F0.wireOp",EDGE,"E6");var subQ3=sQuery(id+"F0.wireOp",EDGE,"E5");var subQ4=sQuery(id+"F0.wireOp",EDGE,"E4");var subQ5=sQuery(id+"F0.wireOp",EDGE,"E22.filletArc");var subQ6=sQuery(id+"F0.wireOp",EDGE,"E1.bottom");var subQ7=sQuery(id+"F0.wireOp",EDGE,"E1.right");var subQ8=sQuery(id+"F0.wireOp",EDGE,"E1.top");var subQ9=sQuery(id+"F0.wireOp",EDGE,"E1.left");var subQ10=sQuery(id+"F0.wireOp",EDGE,"E23.filletArc");var subQ11=sQuery(id+"F0.wireOp",EDGE,"E24.filletArc");Q0=makeQuery(id+"F2.boolean.opBoolean","SPLIT",FACE,{"disambiguationData":[TD([makeQuery(id+"F1.opExtrude","SWEPT_FACE",FACE,{"disambiguationData":[OSD([subQ6])]})])],"derivedFrom":makeQuery(id+"F1.opExtrude","CAP_FACE",FACE,{"disambiguationData":[OSD([subQ6,subQ8,subQ9,subQ7,subQ4,subQ3,subQ2,subQ1,subQ0,subQ5,subQ10,subQ11])],"isStart":true})});}
            var sketch = newSketch(context, id + "F16", { "sketchPlane" : qUnion([Q0])});
            skLineSegment(sketch, "E79.0.0", {"start": v(70, 90) * mm, "end": v(-70, 90) * mm});
            skArc(sketch, "E79.0.1", {"start": v(-70, 90) * mm, "mid": v(-77.07, 87.07) * mm, "end": v(-80, 80) * mm});
            skLineSegment(sketch, "E79.0.2", {"start": v(-80, 80) * mm, "end": v(-80, -80) * mm});
            skArc(sketch, "E79.0.3", {"start": v(-80, -80) * mm, "mid": v(-77.07, -87.07) * mm, "end": v(-70, -90) * mm});
            skLineSegment(sketch, "E79.0.4", {"start": v(-70, -90) * mm, "end": v(70, -90) * mm});
            skArc(sketch, "E79.0.5", {"start": v(70, -90) * mm, "mid": v(77.07, -87.07) * mm, "end": v(80, -80) * mm});
            skLineSegment(sketch, "E79.0.6", {"start": v(80, -80) * mm, "end": v(80, 80) * mm});
            skArc(sketch, "E79.0.7", {"start": v(80, 80) * mm, "mid": v(77.07, 87.07) * mm, "end": v(70, 90) * mm});
            skLineSegment(sketch, "E80", {"start": v(-33, 90) * mm, "end": v(-15, 108) * mm});
            skLineSegment(sketch, "E81", {"start": v(-15, 108) * mm, "end": v(-15, 120) * mm});
            skLineSegment(sketch, "E82", {"start": v(33, 90) * mm, "end": v(15, 108) * mm});
            skLineSegment(sketch, "E83", {"start": v(15, 108) * mm, "end": v(15, 120) * mm});
            skArc(sketch, "E84", {"start": v(15, 120) * mm, "mid": v(0, 135) * mm, "end": v(-15, 120) * mm});
            skCircle(sketch, "E85", {"center": v(0, 120) * mm, "radius": 6 * mm});
            skLineSegment(sketch, "E86", {"start": v(0, 120) * mm, "end": v(0, 90) * mm, "construction": true});
            skLineSegment(sketch, "E87", {"start": v(-80, 0) * mm, "end": v(80, 0) * mm, "construction": true});
            skArc(sketch, "E88.MirrorCS", {"start": v(-15, 120) * mm, "mid": v(0, 135) * mm, "end": v(15, 120) * mm});
            skCircle(sketch, "E89.MirrorC", {"center": v(0, -120) * mm, "radius": 6 * mm});
            skLineSegment(sketch, "E90.MirrorCS", {"start": v(-15, -108) * mm, "end": v(-15, -120) * mm});
            skLineSegment(sketch, "E91.MirrorCS", {"start": v(15, -108) * mm, "end": v(15, -120) * mm});
            skArc(sketch, "E92.MirrorCS", {"start": v(-15, -120) * mm, "mid": v(0, -135) * mm, "end": v(15, -120) * mm});
            skLineSegment(sketch, "E93.MirrorCS", {"start": v(-33, -90) * mm, "end": v(-15, -108) * mm});
            skLineSegment(sketch, "E94.MirrorCS", {"start": v(33, -90) * mm, "end": v(15, -108) * mm});
            skArc(sketch, "E95.MirrorCS", {"start": v(15, -120) * mm, "mid": v(0, -135) * mm, "end": v(-15, -120) * mm});
            skLineSegment(sketch, "E96.MirrorCS", {"start": v(0, -120) * mm, "end": v(0, -90) * mm, "construction": true});
            skSolve(sketch);
        }
        {
            var Q0;
            Q0 = qSketchRegion(id + "F16", true);
            var Q1;
            Q1=makeQuery(id+"F1.opExtrude","CAP_FACE",FACE,{"disambiguationData":[OSD([sQuery(id+"F0.wireOp",EDGE,"E1.bottom"),sQuery(id+"F0.wireOp",EDGE,"E1.top"),sQuery(id+"F0.wireOp",EDGE,"E1.left"),sQuery(id+"F0.wireOp",EDGE,"E1.right"),sQuery(id+"F0.wireOp",EDGE,"E4"),sQuery(id+"F0.wireOp",EDGE,"E5"),sQuery(id+"F0.wireOp",EDGE,"E6"),sQuery(id+"F0.wireOp",EDGE,"E7"),sQuery(id+"F0.wireOp",EDGE,"E21.filletArc"),sQuery(id+"F0.wireOp",EDGE,"E22.filletArc"),sQuery(id+"F0.wireOp",EDGE,"E23.filletArc"),sQuery(id+"F0.wireOp",EDGE,"E24.filletArc")])],"isStart":false});
            extrude(context, id + "F17", {"entities" : qUnion([Q0]), "endBound" : BoundingType.UP_TO_SURFACE, "oppositeDirection" : true, "endBoundEntityFace" : qUnion([Q1]), "depth" : 25 * mm});
        }
    });
